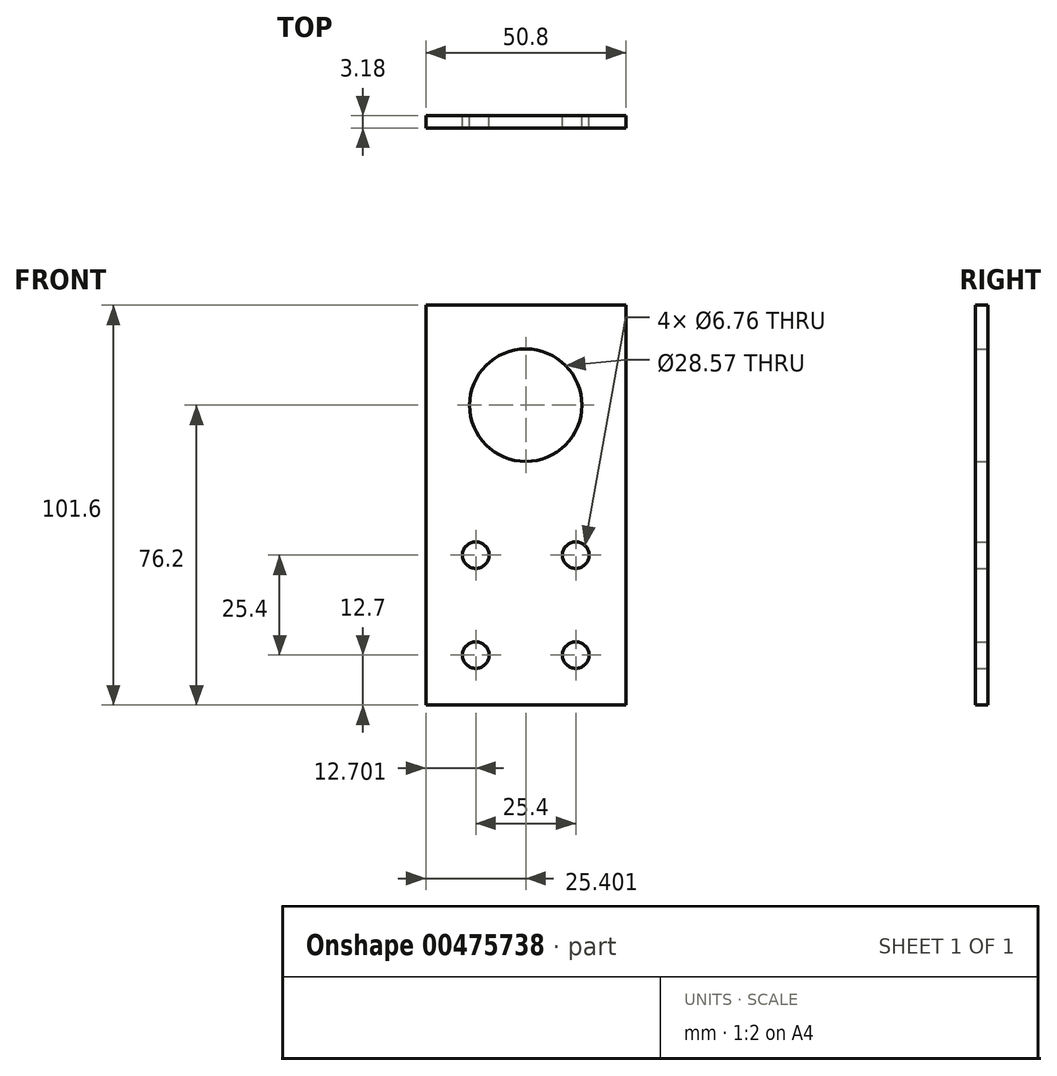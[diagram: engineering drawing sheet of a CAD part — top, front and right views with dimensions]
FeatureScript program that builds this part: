
annotation { "Feature Type Name" : "Feature", "Feature Type Description" : "" }
export const myFeature = defineFeature(function(context is Context, id is Id, definition is map)
    precondition{}
    {
        {
            var Q0;
            Q0=qCreatedBy(makeId("Front.planeOp"),FACE);
            var sketch = newSketch(context, id + "F0", { "sketchPlane" : qUnion([Q0])});
            skLineSegment(sketch, "E0.bottom", {"start": v(-2.52, 95.27) * mm, "end": v(48.28, 95.27) * mm});
            skLineSegment(sketch, "E0.top", {"start": v(-2.52, -6.33) * mm, "end": v(48.28, -6.33) * mm});
            skLineSegment(sketch, "E0.left", {"start": v(-2.52, 95.27) * mm, "end": v(-2.52, -6.33) * mm});
            skLineSegment(sketch, "E0.right", {"start": v(48.28, 95.27) * mm, "end": v(48.28, -6.33) * mm});
            skPoint(sketch, "E1.oppositeSnap0", {"position": v(22.88, 95.27) * mm});
            skCircle(sketch, "E2", {"center": v(22.88, 69.87) * mm, "radius": 14.29 * mm});
            skCircle(sketch, "E3", {"center": v(35.58, 31.77) * mm, "radius": 3.38 * mm});
            skCircle(sketch, "E4", {"center": v(10.18, 31.77) * mm, "radius": 3.38 * mm});
            skCircle(sketch, "E5", {"center": v(10.18, 6.37) * mm, "radius": 3.38 * mm});
            skCircle(sketch, "E6", {"center": v(35.58, 6.37) * mm, "radius": 3.38 * mm});
            skSolve(sketch);
        }
        {
            var Q0;
            Q0 = qSketchRegion(id + "F0", true);
            extrude(context, id + "F1", {"entities" : qUnion([Q0]), "depth" : 3.17 * mm});
        }
    });
